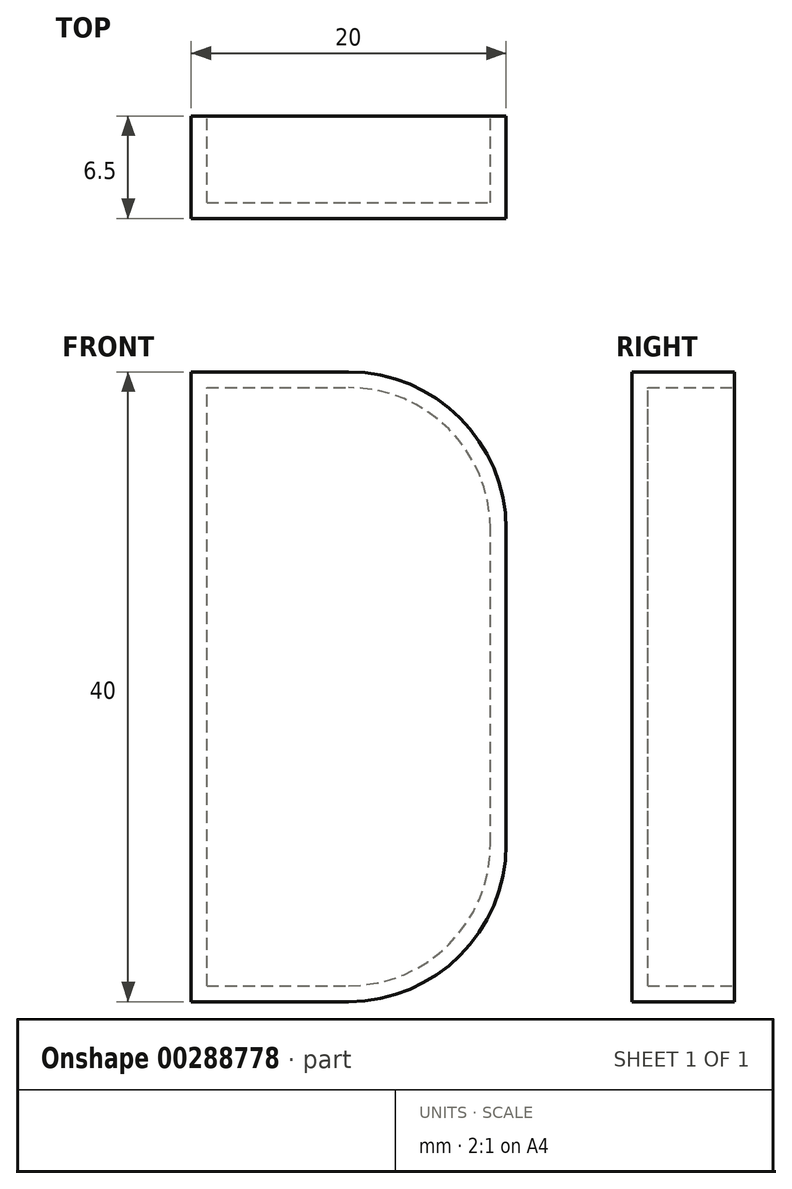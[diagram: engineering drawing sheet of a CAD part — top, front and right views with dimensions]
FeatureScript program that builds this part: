
annotation { "Feature Type Name" : "Feature", "Feature Type Description" : "" }
export const myFeature = defineFeature(function(context is Context, id is Id, definition is map)
    precondition{}
    {
        {
            var Q0;
            Q0=qCreatedBy(makeId("Front.planeOp"),FACE);
            var sketch = newSketch(context, id + "F0", { "sketchPlane" : qUnion([Q0])});
            skLineSegment(sketch, "E0.bottom", {"start": v(-12.37, -18.38) * mm, "end": v(-2.37, -18.38) * mm});
            skLineSegment(sketch, "E0.top", {"start": v(-12.37, 21.62) * mm, "end": v(-2.37, 21.62) * mm});
            skLineSegment(sketch, "E0.left", {"start": v(-12.37, -18.38) * mm, "end": v(-12.37, 21.62) * mm});
            skLineSegment(sketch, "E0.right", {"start": v(7.63, -8.38) * mm, "end": v(7.63, 11.62) * mm});
            skPoint(sketch, "E1.visualSharp", {"position": v(7.63, 21.62) * mm});
            skArc(sketch, "E1.filletArc", {"start": v(7.63, 11.62) * mm, "mid": v(4.7, 18.7) * mm, "end": v(-2.37, 21.62) * mm});
            skPoint(sketch, "E2.visualSharp", {"position": v(7.63, -18.38) * mm});
            skArc(sketch, "E2.filletArc", {"start": v(-2.37, -18.38) * mm, "mid": v(4.7, -15.45) * mm, "end": v(7.63, -8.38) * mm});
            skSolve(sketch);
        }
        {
            var Q0;
            Q0=makeQuery(id+"F0.imprint","IMPRINT",FACE,{"disambiguationData":[TD([[makeQuery(id+"F0.imprint","IMPRINT",EDGE,{"derivedFrom":sQuery(id+"F0.wireOp",EDGE,"E0.bottom")}),1.0]])]});
            extrude(context, id + "F1", {"entities" : qUnion([Q0]), "depth" : 6.5 * mm});
        }
        {
            var Q0;
            Q0=makeQuery(id+"F1.opExtrude","CAP_FACE",FACE,{"disambiguationData":[OSD([sQuery(id+"F0.wireOp",EDGE,"E0.bottom"),sQuery(id+"F0.wireOp",EDGE,"E0.top"),sQuery(id+"F0.wireOp",EDGE,"E0.left"),sQuery(id+"F0.wireOp",EDGE,"E0.right"),sQuery(id+"F0.wireOp",EDGE,"E1.filletArc"),sQuery(id+"F0.wireOp",EDGE,"E2.filletArc")])],"isStart":true});
            shell(context, id + "F2", {"entities" : qUnion([Q0]), "thickness" : 1 * mm});
        }
    });
